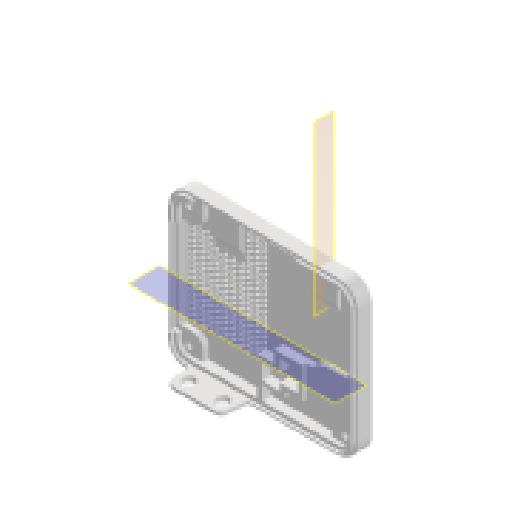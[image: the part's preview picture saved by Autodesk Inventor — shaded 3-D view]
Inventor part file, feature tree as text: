
AUTODESK INVENTOR PART (.ipt)
format: ipt  version: 2025 (Build 290162000, 162)  size: 3,170,304 bytes
history: native  units: mm
features: reference x58, sketch x28, extrude x23, other x14, fillet x6, chamfer x5, mirror x4, plane x2, shell x1, hole x1, pattern_linear x1, sweep x1
ambient origin geometry x8: Origin, YZ Plane, XZ Plane, XY Plane, X Axis, Y Axis, Z Axis, Center Point
bodies: Solid1 (feature_tree)
feature tree (144):
  extrude  "Extrusion1"  Depth=90.0mm
  extrude  "Extrusion2"  Depth=10.0mm
  shell  "Shell1"  Thickness=0.0mm
  extrude  "Extrusion8"  Depth=3.0mm
  extrude  "Extrusion9"  Depth=2.0mm
  extrude  "Extrusion10"  Depth=1.25mm
  extrude  "Extrusion11"  Depth=2.0mm TaperAngle=0.0deg
  extrude  "Extrusion13"  Depth=6.0mm
  fillet  "Fillet3"  Radius=6.0mm
  mirror  "Mirror2"
  mirror  "Mirror3"
  hole  "Hole2"  [1 undecoded]
  extrude  "Toggle_add_mat"  Depth=0.5mm
  extrude  "Toggle_hole"  Depth=3.0mm
  extrude  "Encoder_add_mat"  Depth=5.0mm
  extrude  "Encoder_hole"  Depth=4.0mm
  extrude  "Ventilation_hive"  Depth=2.625mm
  extrude  "Ventilation_vent1"  Depth=2.6mm
  extrude  "Ventilation_vent2"  Depth=1.0mm
  fillet  "Fillet4"  Radius=4.0mm
  extrude  "BTN_support"  TaperAngle=30.0deg  [1 undecoded]
  extrude  "Extrusion22"  Depth=6.0mm
  extrude  "Extrusion23"  Depth=10.0mm TaperAngle=0.0deg
  extrude  "Extrusion24"  Depth=6.0mm
  plane  "Work Plane1"
  extrude  "Extrusion27"  Depth=2.4mm
  mirror  "Mirror5"
  chamfer  "Chamfer3"  Distance=2.4mm
  extrude  "Extrusion28"  Depth=2.0mm
  chamfer  "Chamfer4"  Distance=3.6mm
  extrude  "Extrusion29"  Depth=10.0mm TaperAngle=0.0deg
  mirror  "Mirror6"
  fillet  "Fillet5"  Radius=10.0mm
  pattern_linear  "Rectangular Pattern2"  Spacing1=12.0mm  [1 undecoded]
  chamfer  "Chamfer1"  Distance=12.5mm
  fillet  "Fillet6"  Radius=3.65mm
  extrude  "Extrusion30"  Depth=0.5mm
  fillet  "Fillet7"  Radius=1.5mm
  extrude  "Extrusion31"  Depth=0.5mm TaperAngle=0.0deg
  fillet  "Fillet8"  Radius=4.0mm
  plane  "Work Plane2"
  sweep  "Sweep1"
  chamfer  "Chamfer5"  Distance=0.6mm
  chamfer  "Chamfer6"  Distance=2.5mm
  sketch  "Sketch1"  dims[d0=110.0mm d1=90.0mm]
  sketch  "Sketch2"  dims[d7=3.0mm d21=0.4mm]
  reference  "Reference1"
  reference  "Reference2"
  reference  "Reference3"
  reference  "Reference4"
  reference  "Reference5"
  reference  "Reference6"
  reference  "Reference7"
  reference  "Reference8"
  sketch  "Sketch9"  dims[d25=3.3mm d26=0.0mm d27=1.25mm]
  sketch  "Sketch10"  dims[d28=10.0mm d29=2.0mm d30=0.0mm]
  sketch  "Sketch11"  dims[d31=6.0mm d32=6.0mm d33=6.0mm]
  sketch  "Sketch12"  dims[d34=14.0mm d35=1.6mm d36=0.0mm]
  reference  "Reference38"
  reference  "Reference39"
  sketch  "Sketch16"  dims[d48=3.0mm d49=0.0mm d51=0.5mm]
  reference  "Reference49"
  sketch  "Sketch17"  dims[d52=3.3mm d53=6.0mm d54=5.82mm d55=3.2mm d56=90.0deg d57=8.0mm d58=20.594885mm d60=3.0mm]
  reference  "Reference50"
  reference  "Reference51"
  reference  "Reference52"
  sketch  "Sketch18"  dims[d63=3.0mm d64=5.0mm]
  reference  "Reference53"
  reference  "Reference54"
  reference  "Reference55"
  sketch  "Sketch19"  dims[d65=4.0mm d66=0.0mm d67=0.6mm]
  reference  "Reference56"
  reference  "Reference57"
  sketch  "Sketch20"  dims[d68=2.0mm d69=2.625mm]
  reference  "Reference58"
  sketch  "Sketch21"  dims[d70=5.45mm d71=0.0mm d72=2.6mm]
  reference  "Reference59"
  sketch  "Sketch22"  dims[d73=2.0mm d74=0.0mm d75=1.0mm d76=4.0mm d77=0.0mm]
  sketch  "Sketch Rectangular Pattern1"  dims[d2=10.0mm d3=0.0mm d4=20.0mm d5=0.0mm d6=0.0mm]
  sketch  "Sketch24"  dims[d79=38.0mm d81=30.0deg]
  reference  "Reference62"
  reference  "Reference63"
  reference  "Reference64"
  sketch  "Sketch25"  dims[d82=1.0mm d83=6.0mm]
  reference  "Reference65"
  reference  "Reference66"
  sketch  "Sketch26"  dims[d84=220.0mm d86=3.0mm d87=10.0mm d89=10.0mm d99=5.45mm d100=0.0mm]
  reference  "Reference67"
  reference  "Reference68"
  reference  "Reference69"
  reference  "Reference70"
  reference  "Reference71"
  reference  "Reference72"
  reference  "Reference73"
  reference  "Reference74"
  reference  "Reference75"
  reference  "Reference76"
  reference  "Reference77"
  reference  "Reference78"
  reference  "Reference79"
  reference  "Reference80"
  reference  "Reference81"
  reference  "Reference82"
  reference  "Reference83"
  reference  "Reference84"
  reference  "Reference85"
  reference  "Reference86"
  reference  "Reference87"
  sketch  "Sketch27"  dims[d101=2.4mm d102=0.0mm d103=6.0mm]
  sketch  "Sketch28"  dims[d104=4.0mm d105=3.5mm d106=2.4mm d107=0.0mm]
  sketch  "Sketch29"  dims[d108=2.0mm d109=2.0mm d110=45.0deg d111=1.2mm]
  sketch  "Sketch34"  dims[d112=3.0mm]
  sketch  "Sketch37"  dims[d113=2.0mm]
  reference  "Reference91"
  reference  "Reference92"
  sketch  "Sketch39"  dims[d115=0.6mm]
  reference  "Reference93"
  sketch  "Sketch40"  dims[d116=0.6mm]
  reference  "Reference94"
  reference  "Reference95"
  reference  "Reference96"
  reference  "Reference97"
  sketch  "Sketch41"  dims[d119=2.0mm]
  sketch  "Sketch Rectangular Pattern5"  dims[d22=1.7mm d23=0.0mm d24=2.0mm]
  sketch  "Sketch42"  dims[d120=3.5mm d121=3.6mm d122=10.0mm d123=0.0mm d124=10.0mm d125=0.0mm d126=12.0mm d127=12.5mm d129=3.65mm d130=0.0mm d131=2.5mm d134=1.5mm d135=0.0mm d158=2.6mm d159=0.0mm d163=4.0mm d164=16.0mm d166=0.6mm d169=2.5mm d170=0.15mm d171=11.34464mm d174=3.0mm d175=2.0mm d176=60.0deg d178=4.0mm d179=2.0mm d180=0.0mm d181=2.0mm d182=2.0mm d183=60.0deg d187=0.45mm d189=2.2mm d191=1.5mm d192=1.4505mm d193=0.4mm d194=2.8mm d195=150.0deg d196=10.0mm d197=0.0mm d198=2.0mm d199=1.25mm d200=2.0mm d201=20.0mm d203=55.0mm d204=3.0mm d206=7.5mm d207=0.9mm d208=3.3mm d209=5.0mm d211=20.0mm d220=3.0mm d221=14.835299mm d223=19.05mm d224=2.8mm d225=0.0mm d226=4.0mm d227=1.0mm d228=2.8mm d229=0.0mm d230=2.0mm d239=20.0mm d241=3.0mm d242=130.0mm d244=5.0mm d247=0.0mm d248=0.0mm d249=0.3mm d250=2.0mm d251=45.0deg d252=0.5mm d253=2.0mm d254=45.0deg d231=0.5mm d232=0.872665mm d233=0.5mm d234=0.872665mm]
  reference  "Reference98"
  reference  "Reference99"
  reference  "Reference100"
  reference  "Reference101"
  sketch  "3D Sketch1"
  other  "USB_C_PD_PPS_sink_with_enclosure.iam"
  other  "top_enclosure:1"
  other  "USB_C_PD_PPS_sink:1"
  other  "USB-MICRO-B_V_CMP-2000-05827-1:1"
  other  "FP-USB4085-GF-A-MFG_USB4085-GF-A-1:1"
  other  "USB_C_PD_PPS_sink_BOARD:1"
  other  "1M41T1B5M1QE_1M41T1B5M1QE-1:1"
  other  "Aluminium_knob:1"
  other  "B3F-1075_CMP-003-000047-3:1"
  other  "B3F-1075_CMP-003-000047-3:2"
  other  "B3F-1052_B3F-1052-1:2"
  other  "B3F-1052_B3F-1052-1:1"
  other  "B3F-1052_B3F-1052-1:3"
  other  "tilt_leg:1"
note: 3 required parameter values undecoded (feature->parameter linkage not recoverable at this tier; creation-order binding heuristic only, values carry confidence <= 0.55)
